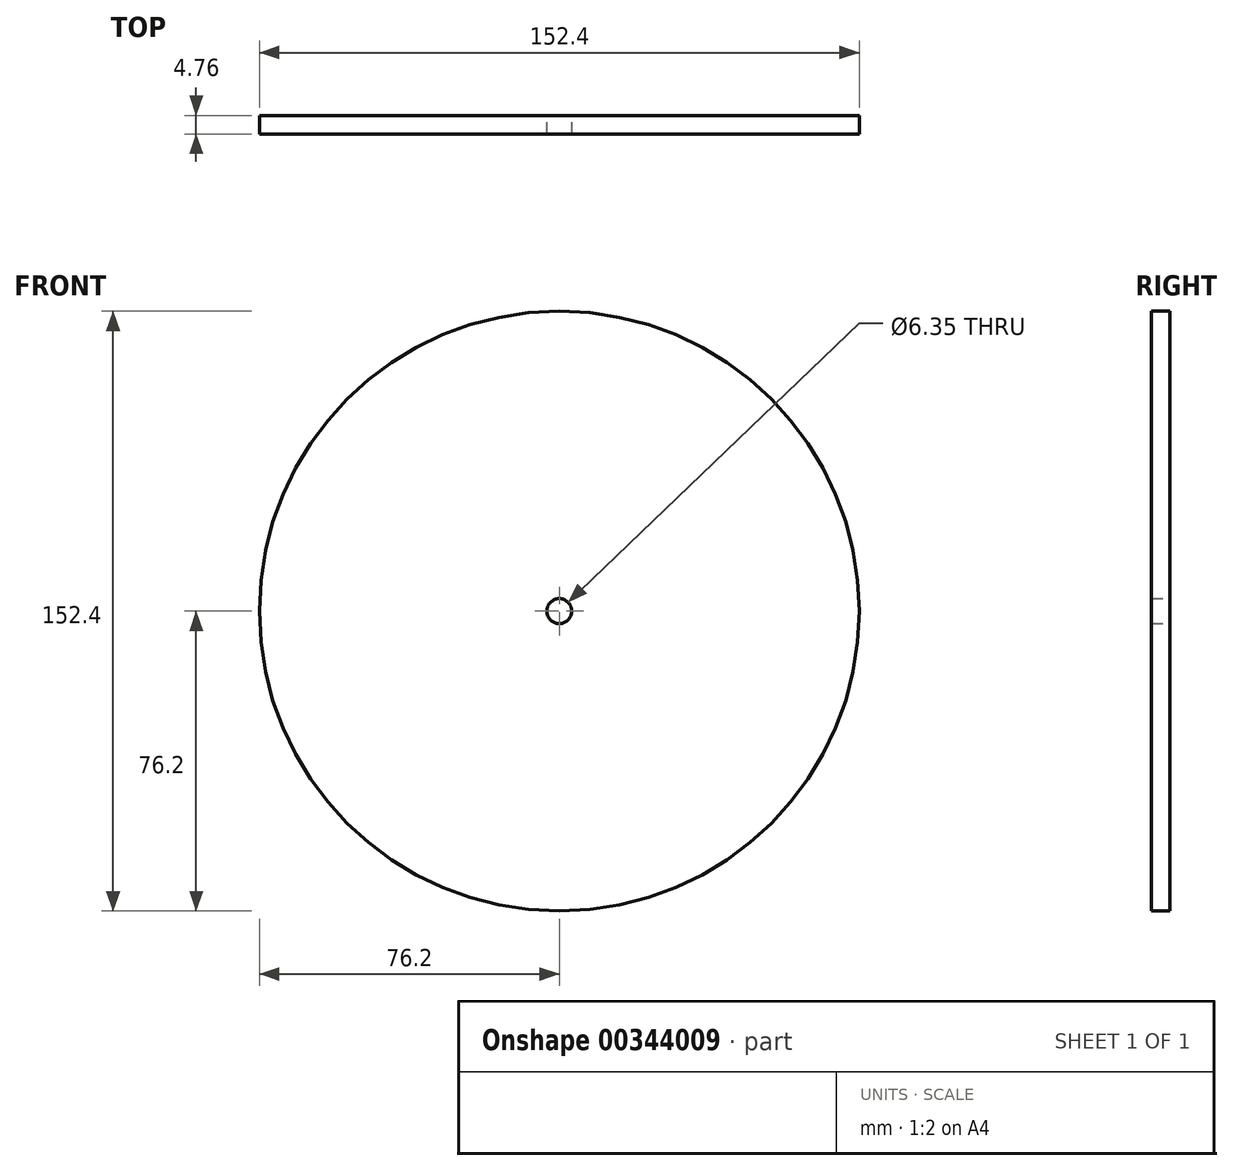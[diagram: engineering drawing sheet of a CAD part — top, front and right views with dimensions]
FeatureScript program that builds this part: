
annotation { "Feature Type Name" : "Feature", "Feature Type Description" : "" }
export const myFeature = defineFeature(function(context is Context, id is Id, definition is map)
    precondition{}
    {
        {
            var Q0;
            Q0=qCreatedBy(makeId("Front.planeOp"),FACE);
            var sketch = newSketch(context, id + "F0", { "sketchPlane" : qUnion([Q0])});
            skCircle(sketch, "E0", {"center": v(0, 0) * mm, "radius": 76.2 * mm});
            skCircle(sketch, "E1", {"center": v(0, 0) * mm, "radius": 3.18 * mm});
            skSolve(sketch);
        }
        {
            var Q0;
            Q0=makeQuery(id+"F0.imprint","IMPRINT",FACE,{"disambiguationData":[TD([[makeQuery(id+"F0.imprint","IMPRINT",EDGE,{"derivedFrom":sQuery(id+"F0.wireOp",EDGE,"E0")}),1.0]])]});
            extrude(context, id + "F1", {"entities" : qUnion([Q0]), "depth" : 4.76 * mm});
        }
    });
